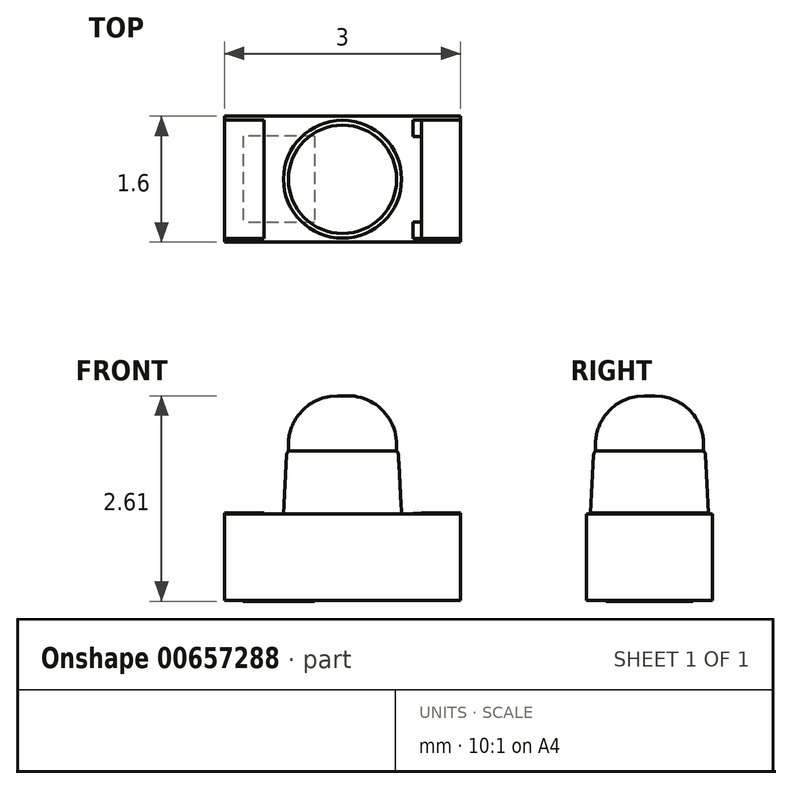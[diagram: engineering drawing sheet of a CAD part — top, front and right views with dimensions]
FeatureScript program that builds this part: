
annotation { "Feature Type Name" : "Feature", "Feature Type Description" : "" }
export const myFeature = defineFeature(function(context is Context, id is Id, definition is map)
    precondition{}
    {
        {
            var Q0;
            Q0=qCreatedBy(makeId("Top.planeOp"),FACE);
            var sketch = newSketch(context, id + "F0", { "sketchPlane" : qUnion([Q0])});
            skLineSegment(sketch, "E0.bottom", {"start": v(1.5, -0.8) * mm, "end": v(-1.5, -0.8) * mm});
            skLineSegment(sketch, "E0.top", {"start": v(1.5, 0.8) * mm, "end": v(-1.5, 0.8) * mm});
            skLineSegment(sketch, "E0.left", {"start": v(1.5, -0.8) * mm, "end": v(1.5, 0.8) * mm});
            skLineSegment(sketch, "E0.right", {"start": v(-1.5, -0.8) * mm, "end": v(-1.5, 0.8) * mm});
            skPoint(sketch, "E0.middle", {"position": v(0, 0) * mm});
            skLineSegment(sketch, "E1.bottom", {"start": v(-1, -0.75) * mm, "end": v(-1.5, -0.75) * mm});
            skLineSegment(sketch, "E1.top", {"start": v(-1, 0.75) * mm, "end": v(-1.5, 0.75) * mm});
            skLineSegment(sketch, "E1.left", {"start": v(-1, -0.75) * mm, "end": v(-1, 0.75) * mm});
            skLineSegment(sketch, "E1.right", {"start": v(-1.5, -0.75) * mm, "end": v(-1.5, 0.75) * mm});
            skPoint(sketch, "E1.middle", {"position": v(-1.25, 0) * mm});
            skLineSegment(sketch, "E2", {"start": v(0, 0.8) * mm, "end": v(0, -0.8) * mm, "construction": true});
            skLineSegment(sketch, "E3.MirrorCS", {"start": v(1, 0.75) * mm, "end": v(1.5, 0.75) * mm});
            skLineSegment(sketch, "E4.MirrorCS", {"start": v(1, -0.75) * mm, "end": v(1, 0.75) * mm});
            skLineSegment(sketch, "E5.MirrorCS", {"start": v(1, -0.75) * mm, "end": v(1.5, -0.75) * mm});
            skLineSegment(sketch, "E6.MirrorCS", {"start": v(1.5, -0.75) * mm, "end": v(1.5, 0.75) * mm});
            skCircle(sketch, "E7", {"center": v(0, 0) * mm, "radius": 0.75 * mm});
            skLineSegment(sketch, "E8.bottom", {"start": v(1, 0.75) * mm, "end": v(0.9, 0.75) * mm});
            skLineSegment(sketch, "E8.top", {"start": v(1, 0.54) * mm, "end": v(0.9, 0.54) * mm});
            skLineSegment(sketch, "E8.left", {"start": v(1, 0.75) * mm, "end": v(1, 0.54) * mm});
            skLineSegment(sketch, "E8.right", {"start": v(0.9, 0.75) * mm, "end": v(0.9, 0.54) * mm});
            skLineSegment(sketch, "E9.bottom", {"start": v(-1.5, 0) * mm, "end": v(1.5, 0) * mm, "construction": true});
            skLineSegment(sketch, "E9.top", {"start": v(-1.5, 0) * mm, "end": v(1.5, 0) * mm, "construction": true});
            skLineSegment(sketch, "E9.left", {"start": v(-1.5, 0) * mm, "end": v(-1.5, 0) * mm});
            skLineSegment(sketch, "E9.right", {"start": v(1.5, 0) * mm, "end": v(1.5, 0) * mm});
            skLineSegment(sketch, "E10.MirrorCS", {"start": v(0.9, -0.75) * mm, "end": v(0.9, -0.54) * mm});
            skLineSegment(sketch, "E11.MirrorCS", {"start": v(1, -0.75) * mm, "end": v(1, -0.54) * mm});
            skLineSegment(sketch, "E12.MirrorCS", {"start": v(1, -0.54) * mm, "end": v(0.9, -0.54) * mm});
            skLineSegment(sketch, "E13.MirrorCS", {"start": v(1, -0.75) * mm, "end": v(0.9, -0.75) * mm});
            skSolve(sketch);
        }
        {
            var Q0;
            Q0=makeQuery(id+"F0.imprint","IMPRINT",FACE,{"disambiguationData":[TD([[makeQuery(id+"F0.imprint","IMPRINT",EDGE,{"derivedFrom":sQuery(id+"F0.wireOp",EDGE,"E1.bottom")}),-1.0]])]});
            var Q1;
            {var subQ6=sQuery(id+"F0.wireOp",EDGE,"E0.bottom");Q1=makeQuery(id+"F0.imprint","IMPRINT",FACE,{"disambiguationData":[TD([[makeQuery(id+"F0.imprint","IMPRINT",EDGE,{"derivedFrom":subQ6}),-1.0]])]});}
            var Q2;
            Q2=makeQuery(id+"F0.imprint","IMPRINT",FACE,{"disambiguationData":[TD([[makeQuery(id+"F0.imprint","IMPRINT",EDGE,{"derivedFrom":sQuery(id+"F0.wireOp",EDGE,"E7")}),1.0]])]});
            var Q3;
            Q3=makeQuery(id+"F0.imprint","IMPRINT",FACE,{"disambiguationData":[TD([[makeQuery(id+"F0.imprint","IMPRINT",EDGE,{"derivedFrom":sQuery(id+"F0.wireOp",EDGE,"E8.bottom")}),1.0]])]});
            var Q4;
            Q4=makeQuery(id+"F0.imprint","IMPRINT",FACE,{"disambiguationData":[TD([[makeQuery(id+"F0.imprint","IMPRINT",EDGE,{"derivedFrom":sQuery(id+"F0.wireOp",EDGE,"E3.MirrorCS")}),-1.0]])]});
            var Q5;
            Q5=makeQuery(id+"F0.imprint","IMPRINT",FACE,{"disambiguationData":[TD([[makeQuery(id+"F0.imprint","IMPRINT",EDGE,{"derivedFrom":sQuery(id+"F0.wireOp",EDGE,"E10.MirrorCS")}),-1.0]])]});
            extrude(context, id + "F1", {"entities" : qUnion([Q0, Q1, Q2, Q3, Q4, Q5]), "depth" : -1.1 * mm, "offsetDistance" : 25 * mm});
        }
        {
            var Q0;
            Q0=makeQuery(id+"F0.imprint","IMPRINT",FACE,{"disambiguationData":[TD([[makeQuery(id+"F0.imprint","IMPRINT",EDGE,{"derivedFrom":sQuery(id+"F0.wireOp",EDGE,"E7")}),1.0]])]});
            extrude(context, id + "F2", {"entities" : qUnion([Q0]), "depth" : 0.8 * mm, "offsetDistance" : 25 * mm, "hasDraft" : true, "draftAngle" : 3 * degree, "draftPullDirection" : true});
        }
        {
            var Q0;
            Q0=makeQuery(id+"F2.opExtrude","CAP_FACE",FACE,{"disambiguationData":[OSD([sQuery(id+"F0.wireOp",EDGE,"E7")])],"isStart":false});
            var sketch = newSketch(context, id + "F3", { "sketchPlane" : qUnion([Q0])});
            skLineSegment(sketch, "E14", {"start": v(-0.7, 0) * mm, "end": v(0.7, 0) * mm, "construction": true});
            skCircle(sketch, "E15", {"center": v(0, 0) * mm, "radius": 0.69 * mm});
            skSolve(sketch);
        }
        {
            var Q0;
            Q0=makeQuery(id+"F0.imprint","IMPRINT",FACE,{"disambiguationData":[TD([[makeQuery(id+"F0.imprint","IMPRINT",EDGE,{"derivedFrom":sQuery(id+"F0.wireOp",EDGE,"E1.bottom")}),-1.0]])]});
            var Q1;
            Q1=makeQuery(id+"F0.imprint","IMPRINT",FACE,{"disambiguationData":[TD([[makeQuery(id+"F0.imprint","IMPRINT",EDGE,{"derivedFrom":sQuery(id+"F0.wireOp",EDGE,"E3.MirrorCS")}),-1.0]])]});
            extrude(context, id + "F4", {"entities" : qUnion([Q0, Q1]), "depth" : 0.01 * mm, "offsetDistance" : 25 * mm});
        }
        {
            var Q0;
            Q0=makeQuery(id+"F0.imprint","IMPRINT",FACE,{"disambiguationData":[TD([[makeQuery(id+"F0.imprint","IMPRINT",EDGE,{"derivedFrom":sQuery(id+"F0.wireOp",EDGE,"E10.MirrorCS")}),-1.0]])]});
            var Q1;
            Q1=makeQuery(id+"F0.imprint","IMPRINT",FACE,{"disambiguationData":[TD([[makeQuery(id+"F0.imprint","IMPRINT",EDGE,{"derivedFrom":sQuery(id+"F0.wireOp",EDGE,"E8.bottom")}),1.0]])]});
            extrude(context, id + "F5", {"entities" : qUnion([Q0, Q1]), "depth" : 0 * mm, "offsetDistance" : 25 * mm});
        }
        {
            var Q0;
            Q0=makeQuery(id+"F3.imprint","IMPRINT",FACE,{"disambiguationData":[TD([[makeQuery(id+"F3.imprint","IMPRINT",EDGE,{"derivedFrom":sQuery(id+"F3.wireOp",EDGE,"E15")}),1.0]])]});
            extrude(context, id + "F6", {"entities" : qUnion([Q0]), "operationType" : NewBodyOperationType.ADD, "depth" : (2.6 - 1.1 - 0.8) * mm, "offsetDistance" : 25 * mm});
        }
        {
            var Q0;
            Q0=makeQuery(id+"F6.opExtrude","CAP_EDGE",EDGE,{"disambiguationData":[OSD([sQuery(id+"F3.wireOp",EDGE,"E15")])],"isStart":false});
            fillet(context, id + "F7", {"entities" : qUnion([Q0]), "radius" : 0.62 * mm, "tangentPropagation" : true, "allowEdgeOverflow" : false});
        }
        {
            var Q0;
            Q0=makeQuery(id+"F2.opExtrude","CAP_EDGE",EDGE,{"disambiguationData":[OSD([sQuery(id+"F0.wireOp",EDGE,"E7")])],"isStart":false});
            fillet(context, id + "F8", {"entities" : qUnion([Q0]), "radius" : 0.09 * mm, "tangentPropagation" : true, "allowEdgeOverflow" : false});
        }
        {
            var Q0;
            Q0=makeQuery(id+"F1.opExtrude","CAP_FACE",FACE,{"disambiguationData":[OSD([sQuery(id+"F0.wireOp",EDGE,"E0.bottom"),sQuery(id+"F0.wireOp",EDGE,"E0.top"),sQuery(id+"F0.wireOp",EDGE,"E0.left"),sQuery(id+"F0.wireOp",EDGE,"E0.right"),sQuery(id+"F0.wireOp",EDGE,"E1.right"),sQuery(id+"F0.wireOp",EDGE,"E6.MirrorCS")])],"isStart":false});
            var sketch = newSketch(context, id + "F9", { "sketchPlane" : qUnion([Q0])});
            skLineSegment(sketch, "E16.bottom", {"start": v(-0.35, -0.55) * mm, "end": v(-1.26, -0.55) * mm});
            skLineSegment(sketch, "E16.top", {"start": v(-0.35, 0.55) * mm, "end": v(-1.26, 0.55) * mm});
            skLineSegment(sketch, "E16.left", {"start": v(-0.35, -0.55) * mm, "end": v(-0.35, 0.55) * mm});
            skLineSegment(sketch, "E16.right", {"start": v(-1.26, -0.55) * mm, "end": v(-1.26, 0.55) * mm});
            skPoint(sketch, "E16.middle", {"position": v(-0.8, 0) * mm});
            skSolve(sketch);
        }
        {
            var Q0;
            Q0=makeQuery(id+"F9.imprint","IMPRINT",FACE,{"disambiguationData":[TD([[makeQuery(id+"F9.imprint","IMPRINT",EDGE,{"derivedFrom":sQuery(id+"F9.wireOp",EDGE,"E16.bottom")}),-1.0]])]});
            extrude(context, id + "F10", {"entities" : qUnion([Q0]), "depth" : 0.01 * mm, "offsetDistance" : 25 * mm});
        }
    });
